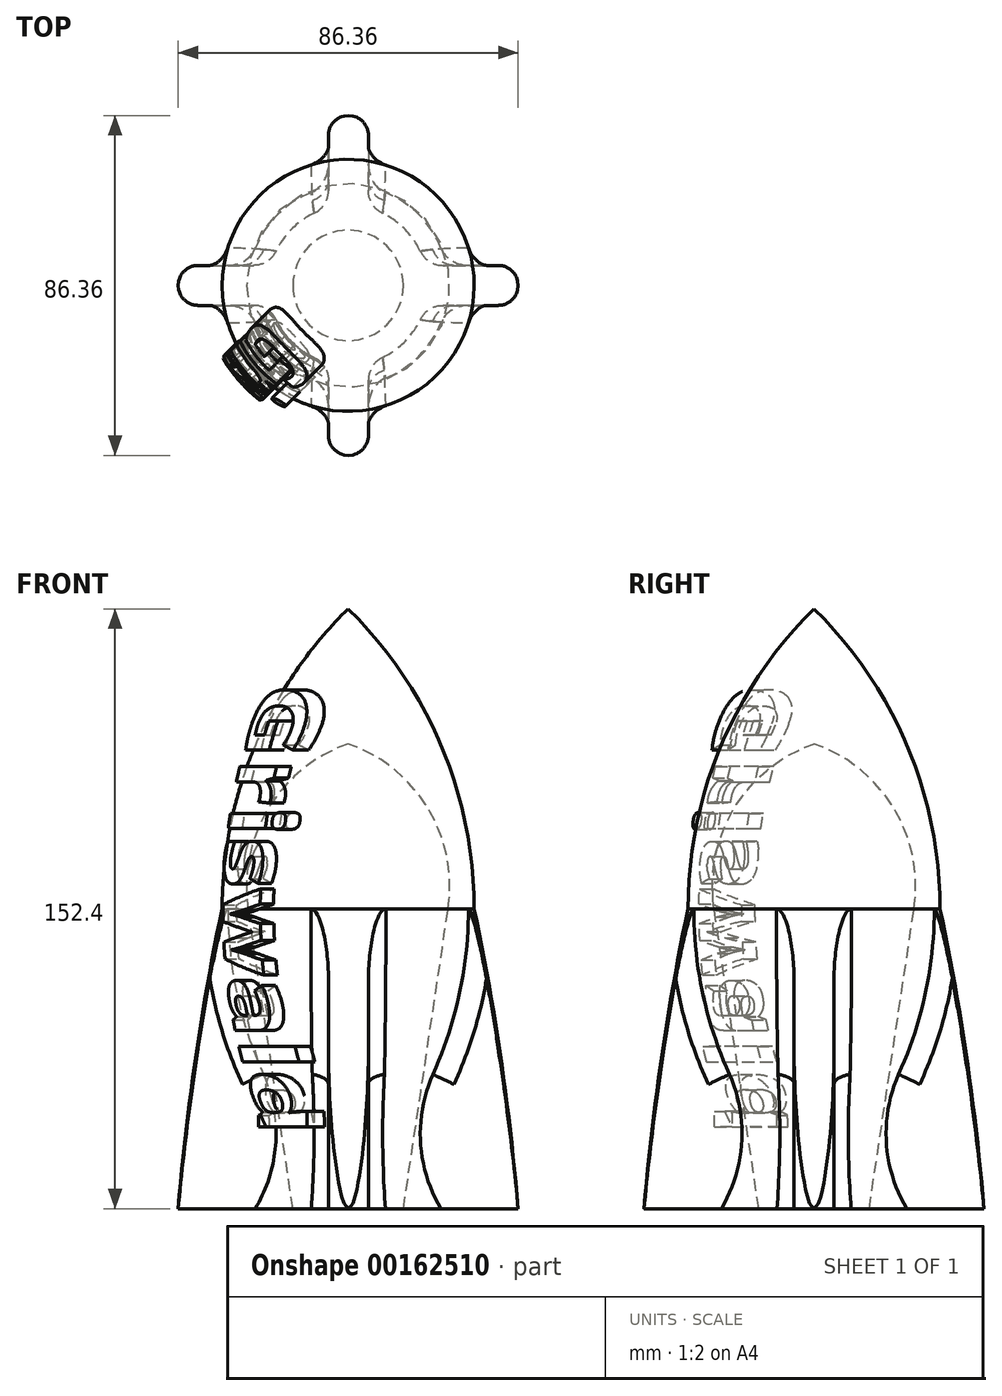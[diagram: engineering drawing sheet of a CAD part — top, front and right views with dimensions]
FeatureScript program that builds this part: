
annotation { "Feature Type Name" : "Feature", "Feature Type Description" : "" }
export const myFeature = defineFeature(function(context is Context, id is Id, definition is map)
    precondition{}
    {
        {
            var Q0;
            Q0=qCreatedBy(makeId("Front.planeOp"),FACE);
            var sketch = newSketch(context, id + "F0", { "sketchPlane" : qUnion([Q0])});
            skArc(sketch, "E0", {"start": v(23.37, -42.09) * mm, "mid": v(30, 20.67) * mm, "end": v(0, 76.2) * mm});
            skLineSegment(sketch, "E1", {"start": v(0, 76.2) * mm, "end": v(0, -76.2) * mm});
            skArc(sketch, "E2", {"start": v(23.37, -42.09) * mm, "mid": v(20.34, -59.38) * mm, "end": v(25.4, -76.2) * mm});
            skLineSegment(sketch, "E3", {"start": v(25.4, -76.2) * mm, "end": v(0, -76.2) * mm});
            skSolve(sketch);
        }
        {
            var Q0;
            Q0=makeQuery(id+"F0.imprint","IMPRINT",FACE,{"disambiguationData":[TD([[makeQuery(id+"F0.imprint","IMPRINT",EDGE,{"derivedFrom":sQuery(id+"F0.wireOp",EDGE,"E0")}),1.0]])]});
            var Q1;
            Q1=sQuery(id+"F0.wireOp",EDGE,"E1");
            revolve(context, id + "F1", {"entities" : qUnion([Q0]), "axis" : qUnion([Q1]), "revolveType" : RevolveType.FULL});
        }
        {
            var Q0;
            Q0=qCreatedBy(makeId("Top.planeOp"),FACE);
            var sketch = newSketch(context, id + "F2", { "sketchPlane" : qUnion([Q0])});
            skLineSegment(sketch, "E4", {"start": v(-38.1, 0) * mm, "end": v(38.1, 0) * mm});
            skLineSegment(sketch, "E5", {"start": v(0, 38.1) * mm, "end": v(0, -44.45) * mm});
            skLineSegment(sketch, "E6.0", {"start": v(0.06, 38.1) * mm, "end": v(0.06, -38.1) * mm});
            skArc(sketch, "E7.0.startCap", {"start": v(-5.02, 38.1) * mm, "mid": v(0.06, 43.18) * mm, "end": v(5.14, 38.1) * mm});
            skArc(sketch, "E7.0.endCap", {"start": v(5.14, -38.1) * mm, "mid": v(0.06, -43.18) * mm, "end": v(-5.02, -38.1) * mm});
            skLineSegment(sketch, "E7.0.left", {"start": v(5.14, 38.1) * mm, "end": v(5.14, -38.1) * mm});
            skLineSegment(sketch, "E7.0.right", {"start": v(-5.02, 38.1) * mm, "end": v(-5.02, -38.1) * mm});
            skArc(sketch, "E8.0.startCap", {"start": v(-38.1, -5.08) * mm, "mid": v(-43.18, 0) * mm, "end": v(-38.1, 5.08) * mm});
            skArc(sketch, "E8.0.endCap", {"start": v(38.1, 5.08) * mm, "mid": v(43.18, 0) * mm, "end": v(38.1, -5.08) * mm});
            skLineSegment(sketch, "E8.0.left", {"start": v(-38.1, 5.08) * mm, "end": v(38.1, 5.08) * mm});
            skLineSegment(sketch, "E8.0.right", {"start": v(-38.1, -5.08) * mm, "end": v(38.1, -5.08) * mm});
            skSolve(sketch);
        }
        {
            var Q0;
            Q0 = qSketchRegion(id + "F2", true);
            var Q1;
            Q1=makeQuery(id+"F1.opRevolve","SWEPT_FACE",FACE,{"disambiguationData":[OSD([sQuery(id+"F0.wireOp",EDGE,"E3")])]});
            extrude(context, id + "F3", {"entities" : qUnion([Q0]), "operationType" : NewBodyOperationType.ADD, "endBound" : BoundingType.UP_TO_SURFACE, "oppositeDirection" : true, "endBoundEntityFace" : qUnion([Q1]), "depth" : 38.1 * mm, "offsetDistance" : 25.4 * mm});
        }
        {
            var Q0;
            Q0=qCreatedBy(makeId("Right.planeOp"),FACE);
            var sketch = newSketch(context, id + "F4", { "sketchPlane" : qUnion([Q0])});
            skArc(sketch, "E9", {"start": v(-32.02, 0) * mm, "mid": v(-38.81, -37.92) * mm, "end": v(-43.18, -76.2) * mm});
            skLineSegment(sketch, "E10", {"start": v(-43.18, -76.2) * mm, "end": v(-54.48, -76.2) * mm});
            skLineSegment(sketch, "E11", {"start": v(-54.48, -76.2) * mm, "end": v(-54.48, 0) * mm});
            skLineSegment(sketch, "E12", {"start": v(-54.48, 0) * mm, "end": v(-32.02, 0) * mm});
            skLineSegment(sketch, "E13", {"start": v(0, 0) * mm, "end": v(0, -94.11) * mm});
            skSolve(sketch);
        }
        {
            var Q0;
            Q0=makeQuery(id+"F4.imprint","IMPRINT",FACE,{"disambiguationData":[TD([[makeQuery(id+"F4.imprint","IMPRINT",EDGE,{"derivedFrom":sQuery(id+"F4.wireOp",EDGE,"E9")}),-1.0]])]});
            var Q1;
            Q1=sQuery(id+"F4.wireOp",EDGE,"E13");
            revolve(context, id + "F5", {"operationType" : NewBodyOperationType.REMOVE, "entities" : qUnion([Q0]), "axis" : qUnion([Q1]), "revolveType" : RevolveType.FULL, "oppositeDirection" : true});
        }
        {
            var Q0;
            {var subQ0=sQuery(id+"F2.wireOp",EDGE,"E8.0.right");Q0=makeQuery(id+"F3.boolean.opBoolean","INTERSECT",EDGE,{"derivedFrom":[makeQuery(id+"F1.opRevolve","SWEPT_FACE",FACE,{"disambiguationData":[OSD([sQuery(id+"F0.wireOp",EDGE,"E0")])]}),makeQuery(id+"F3.opExtrude","SWEPT_FACE",FACE,{"disambiguationData":[OSD([subQ0]),TDD([makeQuery(id+"F2.imprint","IMPRINT",EDGE,{"disambiguationData":[TD([[makeQuery(id+"F2.imprint","INTERSECT",VERTEX,{"derivedFrom":[sQuery(id+"F2.wireOp",EDGE,"E8.0.startCap"),subQ0]}),-1.0]])],"derivedFrom":subQ0})])]})]});}
            var Q1;
            {var subQ0=sQuery(id+"F2.wireOp",EDGE,"E7.0.right");Q1=makeQuery(id+"F3.boolean.opBoolean","INTERSECT",EDGE,{"derivedFrom":[makeQuery(id+"F1.opRevolve","SWEPT_FACE",FACE,{"disambiguationData":[OSD([sQuery(id+"F0.wireOp",EDGE,"E2")])]}),makeQuery(id+"F3.opExtrude","SWEPT_FACE",FACE,{"disambiguationData":[OSD([subQ0]),TDD([makeQuery(id+"F2.imprint","IMPRINT",EDGE,{"disambiguationData":[TD([[makeQuery(id+"F2.imprint","INTERSECT",VERTEX,{"derivedFrom":[sQuery(id+"F2.wireOp",EDGE,"E7.0.endCap"),subQ0]}),1.0]])],"derivedFrom":subQ0})])]})]});}
            var Q2;
            {var subQ0=sQuery(id+"F2.wireOp",EDGE,"E7.0.left");Q2=makeQuery(id+"F3.boolean.opBoolean","INTERSECT",EDGE,{"derivedFrom":[makeQuery(id+"F1.opRevolve","SWEPT_FACE",FACE,{"disambiguationData":[OSD([sQuery(id+"F0.wireOp",EDGE,"E2")])]}),makeQuery(id+"F3.opExtrude","SWEPT_FACE",FACE,{"disambiguationData":[OSD([subQ0]),TDD([makeQuery(id+"F2.imprint","IMPRINT",EDGE,{"disambiguationData":[TD([[makeQuery(id+"F2.imprint","INTERSECT",VERTEX,{"derivedFrom":[sQuery(id+"F2.wireOp",EDGE,"E7.0.endCap"),subQ0]}),1.0]])],"derivedFrom":subQ0})])]})]});}
            var Q3;
            {var subQ0=sQuery(id+"F2.wireOp",EDGE,"E8.0.right");Q3=makeQuery(id+"F3.boolean.opBoolean","INTERSECT",EDGE,{"derivedFrom":[makeQuery(id+"F1.opRevolve","SWEPT_FACE",FACE,{"disambiguationData":[OSD([sQuery(id+"F0.wireOp",EDGE,"E2")])]}),makeQuery(id+"F3.opExtrude","SWEPT_FACE",FACE,{"disambiguationData":[OSD([subQ0]),TDD([makeQuery(id+"F2.imprint","IMPRINT",EDGE,{"disambiguationData":[TD([[makeQuery(id+"F2.imprint","INTERSECT",VERTEX,{"derivedFrom":[sQuery(id+"F2.wireOp",EDGE,"E8.0.endCap"),subQ0]}),1.0]])],"derivedFrom":subQ0})])]})]});}
            var Q4;
            {var subQ0=sQuery(id+"F2.wireOp",EDGE,"E8.0.left");Q4=makeQuery(id+"F3.boolean.opBoolean","INTERSECT",EDGE,{"derivedFrom":[makeQuery(id+"F1.opRevolve","SWEPT_FACE",FACE,{"disambiguationData":[OSD([sQuery(id+"F0.wireOp",EDGE,"E2")])]}),makeQuery(id+"F3.opExtrude","SWEPT_FACE",FACE,{"disambiguationData":[OSD([subQ0]),TDD([makeQuery(id+"F2.imprint","IMPRINT",EDGE,{"disambiguationData":[TD([[makeQuery(id+"F2.imprint","INTERSECT",VERTEX,{"derivedFrom":[sQuery(id+"F2.wireOp",EDGE,"E8.0.endCap"),subQ0]}),1.0]])],"derivedFrom":subQ0})])]})]});}
            var Q5;
            {var subQ0=sQuery(id+"F2.wireOp",EDGE,"E7.0.left");Q5=makeQuery(id+"F3.boolean.opBoolean","INTERSECT",EDGE,{"derivedFrom":[makeQuery(id+"F1.opRevolve","SWEPT_FACE",FACE,{"disambiguationData":[OSD([sQuery(id+"F0.wireOp",EDGE,"E2")])]}),makeQuery(id+"F3.opExtrude","SWEPT_FACE",FACE,{"disambiguationData":[OSD([subQ0]),TDD([makeQuery(id+"F2.imprint","IMPRINT",EDGE,{"disambiguationData":[TD([[makeQuery(id+"F2.imprint","INTERSECT",VERTEX,{"derivedFrom":[sQuery(id+"F2.wireOp",EDGE,"E7.0.startCap"),subQ0]}),-1.0]])],"derivedFrom":subQ0})])]})]});}
            var Q6;
            {var subQ0=sQuery(id+"F2.wireOp",EDGE,"E7.0.right");Q6=makeQuery(id+"F3.boolean.opBoolean","INTERSECT",EDGE,{"derivedFrom":[makeQuery(id+"F1.opRevolve","SWEPT_FACE",FACE,{"disambiguationData":[OSD([sQuery(id+"F0.wireOp",EDGE,"E2")])]}),makeQuery(id+"F3.opExtrude","SWEPT_FACE",FACE,{"disambiguationData":[OSD([subQ0]),TDD([makeQuery(id+"F2.imprint","IMPRINT",EDGE,{"disambiguationData":[TD([[makeQuery(id+"F2.imprint","INTERSECT",VERTEX,{"derivedFrom":[sQuery(id+"F2.wireOp",EDGE,"E7.0.startCap"),subQ0]}),-1.0]])],"derivedFrom":subQ0})])]})]});}
            var Q7;
            {var subQ0=sQuery(id+"F2.wireOp",EDGE,"E8.0.left");Q7=makeQuery(id+"F3.boolean.opBoolean","INTERSECT",EDGE,{"derivedFrom":[makeQuery(id+"F1.opRevolve","SWEPT_FACE",FACE,{"disambiguationData":[OSD([sQuery(id+"F0.wireOp",EDGE,"E2")])]}),makeQuery(id+"F3.opExtrude","SWEPT_FACE",FACE,{"disambiguationData":[OSD([subQ0]),TDD([makeQuery(id+"F2.imprint","IMPRINT",EDGE,{"disambiguationData":[TD([[makeQuery(id+"F2.imprint","INTERSECT",VERTEX,{"derivedFrom":[sQuery(id+"F2.wireOp",EDGE,"E8.0.startCap"),subQ0]}),-1.0]])],"derivedFrom":subQ0})])]})]});}
            fillet(context, id + "F6", {"entities" : qUnion([Q0, Q1, Q2, Q3, Q4, Q5, Q6, Q7]), "radius" : 6.35 * mm, "tangentPropagation" : true, "allowEdgeOverflow" : false});
        }
        {
            var Q0;
            Q0=qCreatedBy(makeId("Front.planeOp"),FACE);
            var Q1;
            Q1=qCreatedBy(makeId("Right.planeOp"),FACE);
            cPlane(context, id + "F7", {"entities" : qUnion([Q0, Q1]), "cplaneType" : CPlaneType.MID_PLANE, "offset" : 25.4 * mm, "width" : 152.4 * mm, "height" : 152.4 * mm});
        }
        {
            var Q0;
            Q0=qCreatedBy(id+"F7.planeOp",FACE);
            var sketch = newSketch(context, id + "F8", { "sketchPlane" : qUnion([Q0])});
            skText(sketch, "E14", { "text": "Griswald", "fontName": "OpenSans-Bold.ttf"});
            const initialGuessF8  = {"E14": [-0.00943, 0.05715, 0, -1, 0.01885]};
            skSetInitialGuess(sketch, initialGuessF8);
            skSolve(sketch);
        }
        {
            var Q0;
            Q0 = qSketchRegion(id + "F8", true);
            extrude(context, id + "F9", {"entities" : qUnion([Q0]), "operationType" : NewBodyOperationType.ADD, "depth" : 48.5 * mm, "offsetDistance" : 25.4 * mm});
        }
        {
            var Q0;
            Q0=qCreatedBy(makeId("Right.planeOp"),FACE);
            var Q1;
            Q1=qCreatedBy(makeId("Front.planeOp"),FACE);
            cPlane(context, id + "F10", {"entities" : qUnion([Q0, Q1]), "cplaneType" : CPlaneType.MID_PLANE, "offset" : 25.4 * mm, "flipAlignment" : true, "width" : 152.4 * mm, "height" : 152.4 * mm});
        }
        {
            var Q0;
            Q0=qCreatedBy(id+"F10.planeOp",FACE);
            var sketch = newSketch(context, id + "F11", { "sketchPlane" : qUnion([Q0])});
            skArc(sketch, "E15", {"start": v(-19.3, 60.9) * mm, "mid": v(-36.75, 2.3) * mm, "end": v(-21.66, -56.95) * mm});
            skLineSegment(sketch, "E16", {"start": v(-21.66, -56.95) * mm, "end": v(-64.57, -56.95) * mm});
            skLineSegment(sketch, "E17", {"start": v(-64.57, -56.95) * mm, "end": v(-64.57, 59.34) * mm});
            skLineSegment(sketch, "E18", {"start": v(-64.57, 59.34) * mm, "end": v(-19.3, 60.9) * mm});
            skLineSegment(sketch, "E19", {"start": v(0, 0) * mm, "end": v(0, -109.47) * mm});
            skSolve(sketch);
        }
        {
            var Q0;
            Q0=makeQuery(id+"F11.imprint","IMPRINT",FACE,{"disambiguationData":[TD([[makeQuery(id+"F11.imprint","IMPRINT",EDGE,{"derivedFrom":sQuery(id+"F11.wireOp",EDGE,"E15")}),-1.0]])]});
            var Q1;
            Q1=sQuery(id+"F11.wireOp",EDGE,"E19");
            revolve(context, id + "F12", {"operationType" : NewBodyOperationType.REMOVE, "entities" : qUnion([Q0]), "axis" : qUnion([Q1]), "revolveType" : RevolveType.SYMMETRIC, "oppositeDirection" : true, "angle" : 45 * degree});
        }
        {
            var Q0;
            Q0=qCreatedBy(makeId("Front.planeOp"),FACE);
            var sketch = newSketch(context, id + "F13", { "sketchPlane" : qUnion([Q0])});
            skLineSegment(sketch, "E20", {"start": v(0, -85.1) * mm, "end": v(12.7, -85.1) * mm});
            skLineSegment(sketch, "E21", {"start": v(12.7, -85.1) * mm, "end": v(25.4, 0) * mm});
            skLineSegment(sketch, "E22", {"start": v(0, -85.1) * mm, "end": v(0, 0) * mm});
            skLineSegment(sketch, "E23", {"start": v(0, 0) * mm, "end": v(0, 41.91) * mm});
            skArc(sketch, "E24", {"start": v(25.4, 0) * mm, "mid": v(20.27, 25.54) * mm, "end": v(0, 41.91) * mm});
            skPoint(sketch, "E25.center.orphan", {"position": v(0, 0) * mm});
            skPoint(sketch, "E25.start.orphan", {"position": v(0, -31.75) * mm});
            skSolve(sketch);
        }
        {
            var Q0;
            Q0 = qSketchRegion(id + "F13", true);
            var Q1;
            Q1=sQuery(id+"F13.wireOp",EDGE,"E22");
            revolve(context, id + "F14", {"operationType" : NewBodyOperationType.REMOVE, "entities" : qUnion([Q0]), "axis" : qUnion([Q1]), "revolveType" : RevolveType.FULL, "oppositeDirection" : true});
        }
    });
